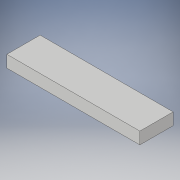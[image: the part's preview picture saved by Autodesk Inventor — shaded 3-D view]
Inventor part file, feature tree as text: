
AUTODESK INVENTOR PART (.ipt)
format: ipt  version: 2018 (Build 220112000, 112)  size: 90,112 bytes
history: native  units: in
note: dims shown in document units (in); Inventor stores cm internally (conversion verified against a paired STEP export)
features: extrude x1, sketch x1
ambient origin geometry x8: Origin, YZ Plane, XZ Plane, XY Plane, X Axis, Y Axis, Z Axis, Center Point
bodies: Solid1 (feature_tree)
feature tree (2):
  extrude  "Extrusion1"  Depth=1.9685in
  sketch  "Sketch1"  dims[d0=7.874in d1=1.9685in d2=0.7087in d3=0.0in]
